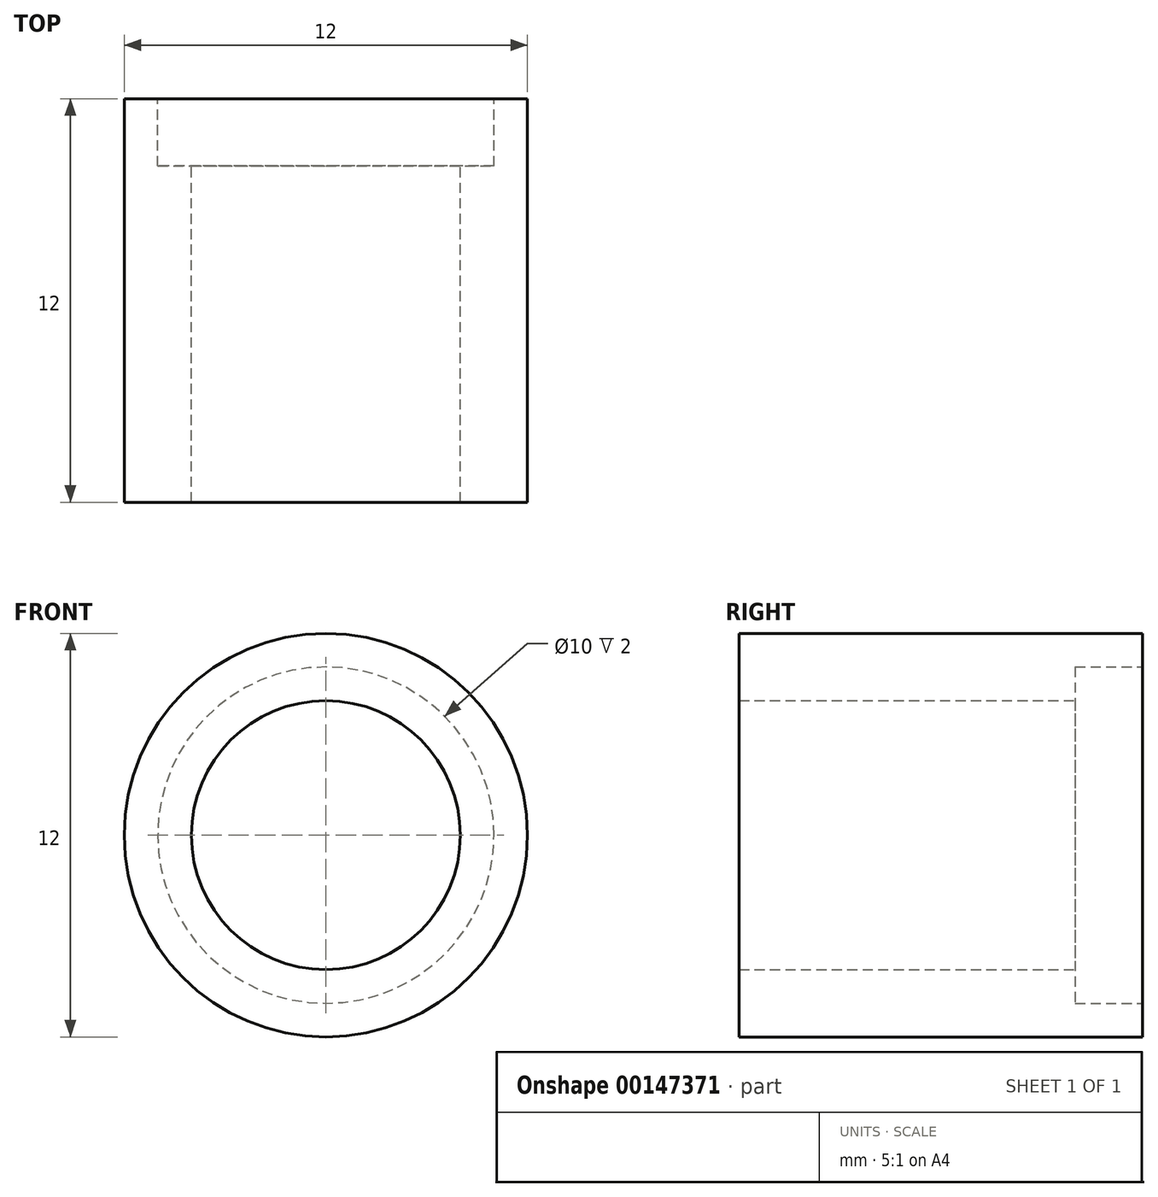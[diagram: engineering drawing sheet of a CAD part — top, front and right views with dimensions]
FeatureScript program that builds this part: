
annotation { "Feature Type Name" : "Feature", "Feature Type Description" : "" }
export const myFeature = defineFeature(function(context is Context, id is Id, definition is map)
    precondition{}
    {
        {
            var Q0;
            Q0=qCreatedBy(makeId("Front.planeOp"),FACE);
            var sketch = newSketch(context, id + "F0", { "sketchPlane" : qUnion([Q0])});
            skCircle(sketch, "E0", {"center": v(0, 0) * mm, "radius": 6 * mm});
            skCircle(sketch, "E1", {"center": v(0, 0) * mm, "radius": 4 * mm});
            skSolve(sketch);
        }
        {
            var Q0;
            Q0 = qSketchRegion(id + "F0", true);
            extrude(context, id + "F1", {"entities" : qUnion([Q0]), "depth" : 12 * mm});
        }
        {
            var Q0;
            Q0=makeQuery(id+"F1.opExtrude","CAP_FACE",FACE,{"disambiguationData":[OSD([sQuery(id+"F0.wireOp",EDGE,"E0"),sQuery(id+"F0.wireOp",EDGE,"E1")])],"isStart":true});
            var sketch = newSketch(context, id + "F2", { "sketchPlane" : qUnion([Q0])});
            skCircle(sketch, "E2", {"center": v(0, 0) * mm, "radius": 5 * mm});
            skSolve(sketch);
        }
        {
            var Q0;
            Q0 = qSketchRegion(id + "F2", true);
            extrude(context, id + "F3", {"entities" : qUnion([Q0]), "operationType" : NewBodyOperationType.REMOVE, "oppositeDirection" : true, "depth" : 2 * mm});
        }
    });
